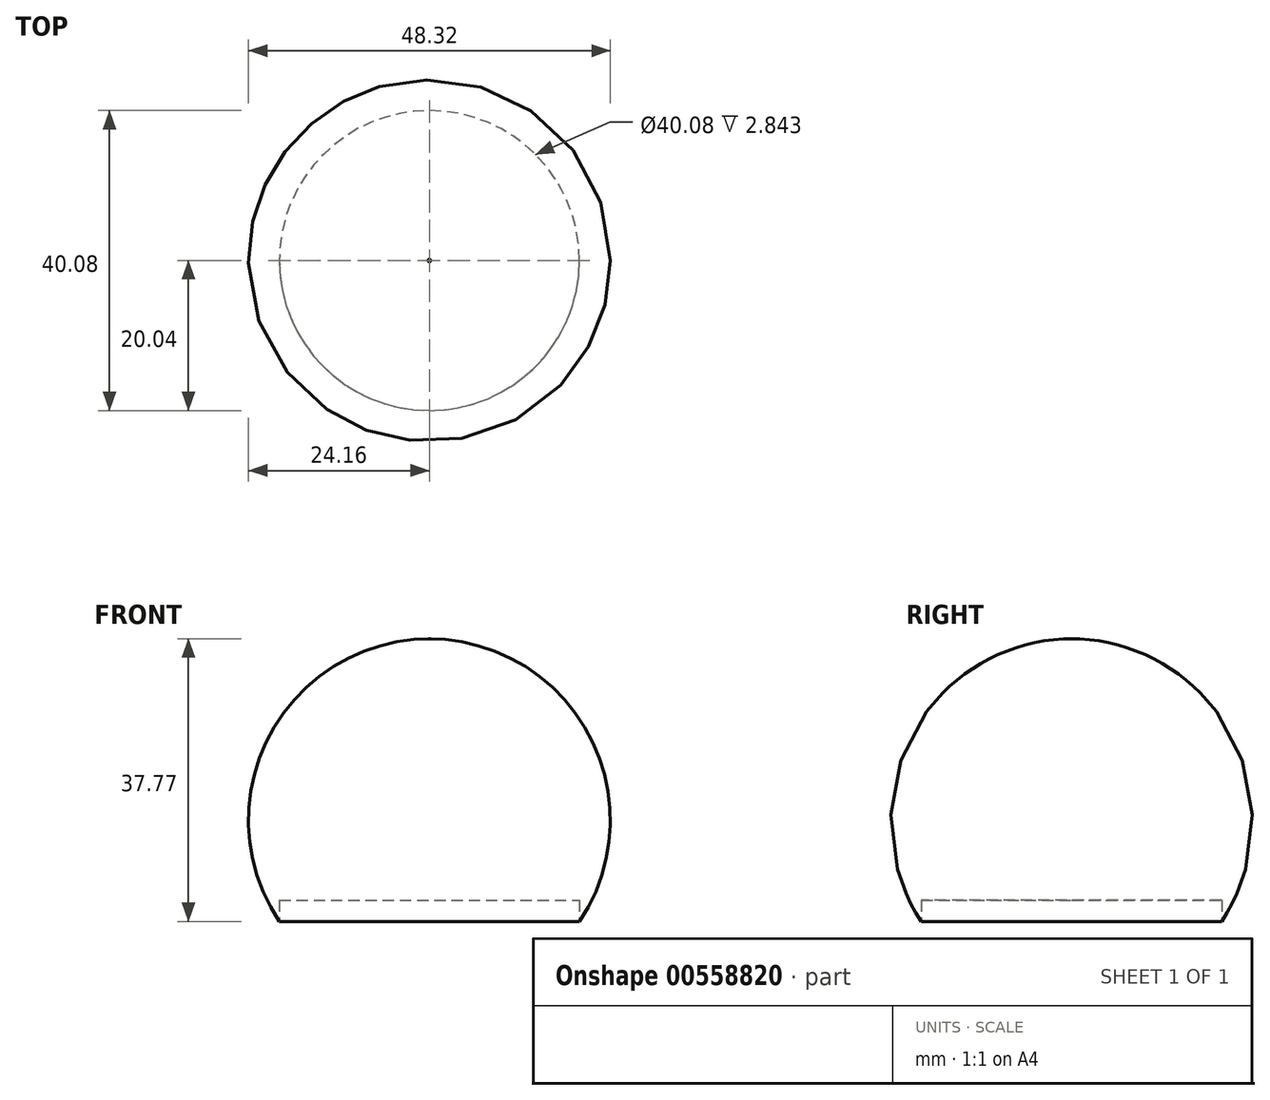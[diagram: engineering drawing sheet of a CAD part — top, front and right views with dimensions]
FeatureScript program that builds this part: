
annotation { "Feature Type Name" : "Feature", "Feature Type Description" : "" }
export const myFeature = defineFeature(function(context is Context, id is Id, definition is map)
    precondition{}
    {
        {
            var Q0;
            Q0=qCreatedBy(makeId("Front.planeOp"),FACE);
            var sketch = newSketch(context, id + "F0", { "sketchPlane" : qUnion([Q0])});
            skArc(sketch, "E0", {"start": v(20.04, 34.97) * mm, "mid": v(21.33, 59.86) * mm, "end": v(0, 72.74) * mm});
            skLineSegment(sketch, "E1", {"start": v(-0.1, 48.5) * mm, "end": v(-0.1, -107.19) * mm, "construction": true});
            skLineSegment(sketch, "E2.bottom", {"start": v(20.04, 37.81) * mm, "end": v(-0.1, 37.81) * mm, "construction": true});
            skLineSegment(sketch, "E2.left", {"start": v(20.04, 37.81) * mm, "end": v(20.04, 34.97) * mm, "construction": true});
            skLineSegment(sketch, "E3", {"start": v(20.04, 37.81) * mm, "end": v(20.04, 34.97) * mm});
            skLineSegment(sketch, "E4", {"start": v(-0.1, 37.81) * mm, "end": v(20.04, 37.81) * mm});
            skLineSegment(sketch, "E5", {"start": v(0, 0) * mm, "end": v(0, 97.11) * mm});
            skSolve(sketch);
        }
        {
            var Q0;
            {var subQ0=sQuery(id+"F0.wireOp",EDGE,"E0");Q0=makeQuery(id+"F0.imprint","IMPRINT",FACE,{"disambiguationData":[TD([[makeQuery(id+"F0.imprint","IMPRINT",EDGE,{"derivedFrom":subQ0}),1.0]])]});}
            var Q1;
            Q1=sQuery(id+"F0.wireOp",EDGE,"E5");
            revolve(context, id + "F1", {"entities" : qUnion([Q0]), "axis" : qUnion([Q1]), "revolveType" : RevolveType.FULL});
        }
    });
